# Revit family: Sanitary_Showers_AXOR_36733XXX-AXOR-ShowerSolutions-Porter-uni222
name_source: partatom
category: Plumbing Fixtures
revit_build: Autodesk Revit 2018 (Build: 20170223_1515(x64)
units: mm (PartAtom-declared; Revit-internal decimal feet)

## family parameters
Always vertical = No
Cut with Voids When Loaded = No
OmniClass Number = 23.31.17.19
OmniClass Title = Shower Head Fixtures
Part Type = Normal
Room Calculation Point = No
Round Connector Dimension = Use Diameter
Shared = No
Work Plane-Based = Yes

## types (1)
- Default - please load Revit Family Type Catalog
    Always visible = Yes
    BIMobject category = Showers
    Default Elevation = 1219.2 mm
    Description = AXOR ShowerSolutions Porter unit round
    Design country = Germany
    EAN code = 4059625031957
    Edition number = 1
    GTIN code = https://4059625031957
    IFC Classification = Sanitary Terminal
    Installation instructions = https://www.axor-design.com
    Manufacturer = AXOR
    Manufacturer country = Germany
    Manufacturer name = AXOR
    Material 1 = AXOR - Plastic - Gray
    Material 2 = AXOR - Metal - 000 Chrome
    Model = 36733XXX
    OmniClass Code = 23-31 17 19
    OmniClass Description = Shower Head Fixtures
    Product Guid = 7f2fc2ea-bf3c-4734-af0c-3b14b4413812
    Product SKU = 36733XXX
    Product data url = https://www.bimobject.com
    Product family = AXOR ShowerSolutions
    Product group = Wall outlet
    Product name = 36733XXX AXOR ShowerSolutions Porter unit round
    Product url = https://www.axor-design.com
    QR code = https://www.bimobject.com
    URL = https://www.axor-design.com
    Water Inlet = 13 mm
    Water Inlet Description = Water Inlet 12.7mm
    Weight Net (Kg) = 485

## geometry (parser evidence)
native form markers: Sweep x2
no freeform markers — native parametric forms only
